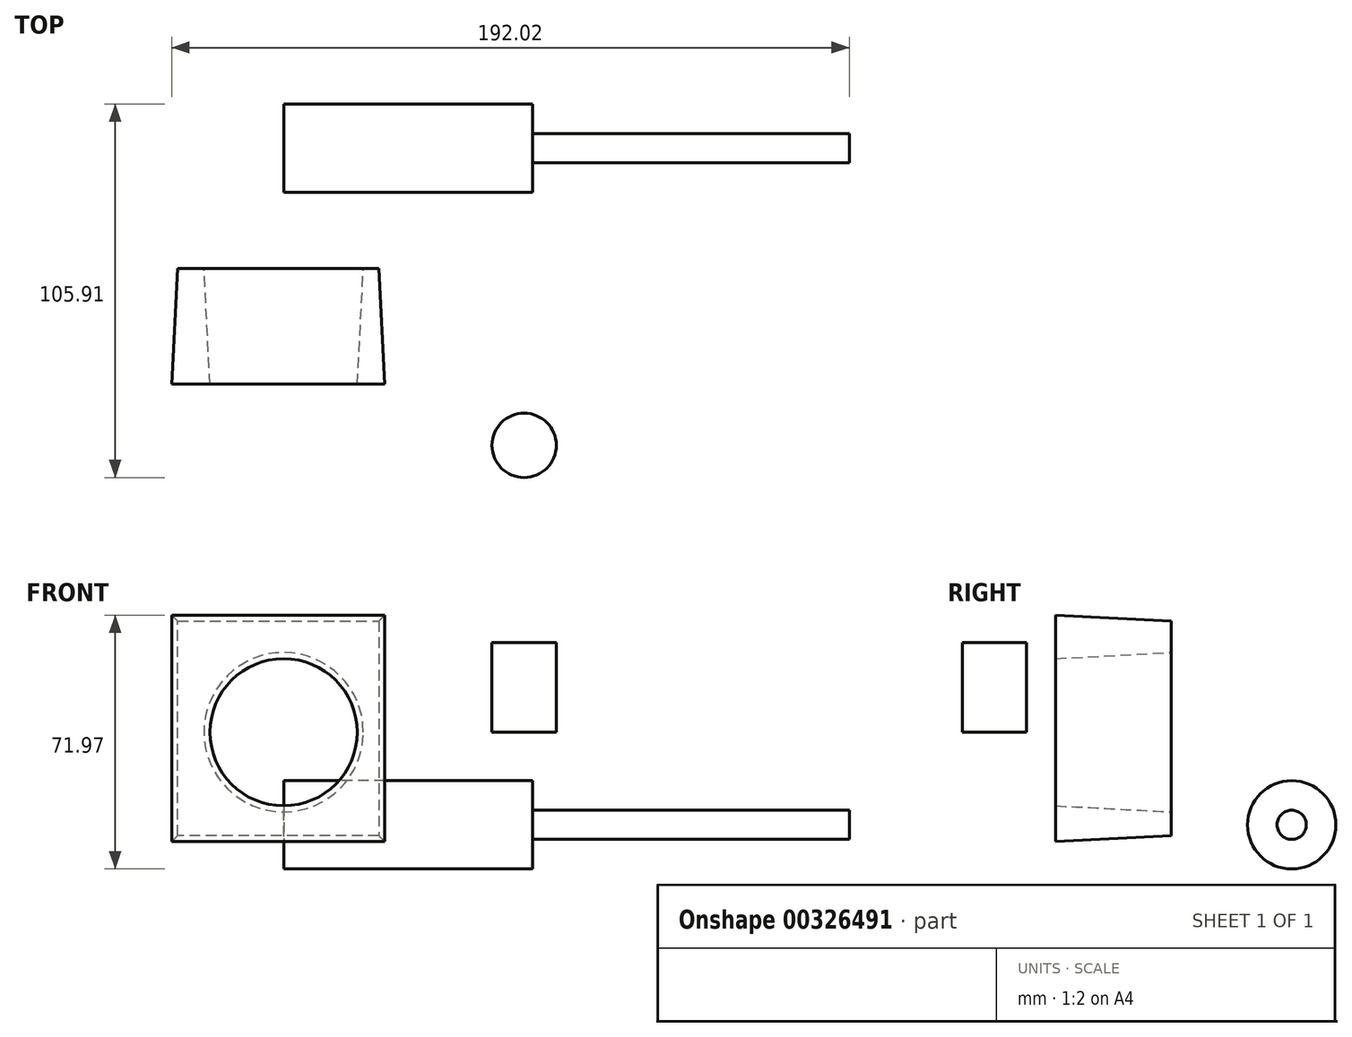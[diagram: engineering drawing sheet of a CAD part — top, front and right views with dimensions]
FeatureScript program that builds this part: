
annotation { "Feature Type Name" : "Feature", "Feature Type Description" : "" }
export const myFeature = defineFeature(function(context is Context, id is Id, definition is map)
    precondition{}
    {
        {
            var Q0;
            Q0=qCreatedBy(makeId("Front.planeOp"),FACE);
            var sketch = newSketch(context, id + "F0", { "sketchPlane" : qUnion([Q0])});
            skCircle(sketch, "E0", {"center": v(0, 0) * mm, "radius": 18.88 * mm});
            skCircle(sketch, "E1", {"center": v(0, 0) * mm, "radius": 22.58 * mm});
            skLineSegment(sketch, "E2.bottom", {"start": v(-30.03, 31.47) * mm, "end": v(26.97, 31.47) * mm});
            skLineSegment(sketch, "E2.top", {"start": v(-30.03, -29.3) * mm, "end": v(26.97, -29.3) * mm});
            skLineSegment(sketch, "E2.left", {"start": v(-30.03, 31.47) * mm, "end": v(-30.03, -29.3) * mm});
            skLineSegment(sketch, "E2.right", {"start": v(26.97, 31.47) * mm, "end": v(26.97, -29.3) * mm});
            skSolve(sketch);
        }
        {
            var Q0;
            Q0 = qSketchRegion(id + "F0", true);
            extrude(context, id + "F1", {"entities" : qUnion([Q0]), "depth" : 32.77 * mm, "hasDraft" : true, "draftAngle" : 3 * degree});
        }
        {
            var Q0;
            Q0=qCreatedBy(makeId("Top.planeOp"),FACE);
            var sketch = newSketch(context, id + "F2", { "sketchPlane" : qUnion([Q0])});
            skCircle(sketch, "E3", {"center": v(68.15, -50.12) * mm, "radius": 9.12 * mm});
            skSolve(sketch);
        }
        {
            var Q0;
            Q0 = qSketchRegion(id + "F2", true);
            extrude(context, id + "F3", {"entities" : qUnion([Q0]), "depth" : 25.4 * mm});
        }
        {
            var Q0;
            Q0=qCreatedBy(makeId("Right.planeOp"),FACE);
            var sketch = newSketch(context, id + "F4", { "sketchPlane" : qUnion([Q0])});
            skCircle(sketch, "E4", {"center": v(34.14, -26.25) * mm, "radius": 12.52 * mm});
            skSolve(sketch);
        }
        {
            var Q0;
            Q0 = qSketchRegion(id + "F4", true);
            extrude(context, id + "F5", {"entities" : qUnion([Q0]), "depth" : 70.61 * mm});
        }
        {
            var Q0;
            Q0=makeQuery(id+"F5.opExtrude","CAP_FACE",FACE,{"disambiguationData":[OSD([sQuery(id+"F4.wireOp",EDGE,"E4")])],"isStart":false});
            var sketch = newSketch(context, id + "F6", { "sketchPlane" : qUnion([Q0])});
            skCircle(sketch, "E5", {"center": v(34.14, -26.25) * mm, "radius": 4.15 * mm});
            skSolve(sketch);
        }
        {
            var Q0;
            Q0 = qSketchRegion(id + "F6", true);
            extrude(context, id + "F7", {"entities" : qUnion([Q0]), "operationType" : NewBodyOperationType.ADD, "depth" : 89.66 * mm});
        }
    });
